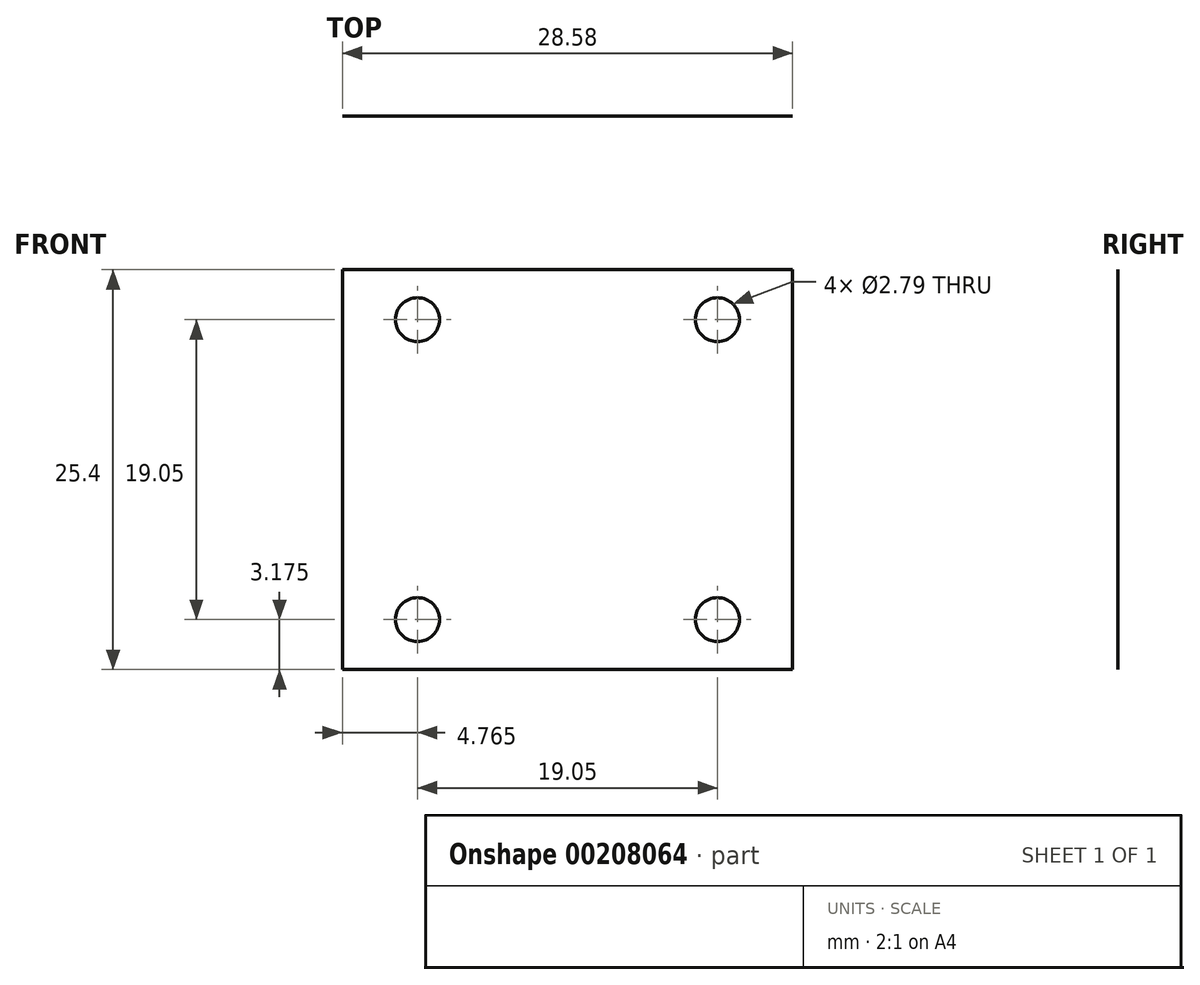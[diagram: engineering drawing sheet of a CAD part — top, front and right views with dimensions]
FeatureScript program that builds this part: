
annotation { "Feature Type Name" : "Feature", "Feature Type Description" : "" }
export const myFeature = defineFeature(function(context is Context, id is Id, definition is map)
    precondition{}
    {
        {
            var Q0;
            Q0=qCreatedBy(makeId("Front.planeOp"),FACE);
            var sketch = newSketch(context, id + "F0", { "sketchPlane" : qUnion([Q0])});
            skLineSegment(sketch, "E0.bottom", {"start": v(14.29, -12.7) * mm, "end": v(-14.29, -12.7) * mm});
            skLineSegment(sketch, "E0.top", {"start": v(14.29, 12.7) * mm, "end": v(-14.29, 12.7) * mm});
            skLineSegment(sketch, "E0.left", {"start": v(14.29, -12.7) * mm, "end": v(14.29, 12.7) * mm});
            skLineSegment(sketch, "E0.right", {"start": v(-14.29, -12.7) * mm, "end": v(-14.29, 12.7) * mm});
            skPoint(sketch, "E0.middle", {"position": v(0, 0) * mm});
            skSolve(sketch);
        }
        {
            var Q0;
            Q0=makeQuery(id+"F0.imprint","IMPRINT",FACE,{"disambiguationData":[TD([[makeQuery(id+"F0.imprint","IMPRINT",EDGE,{"derivedFrom":sQuery(id+"F0.wireOp",EDGE,"E0.bottom")}),-1.0]])]});
            extrude(context, id + "F1", {"entities" : qUnion([Q0]), "depth" : 1 / 203.2 * mm});
        }
        {
            var Q0;
            Q0=makeQuery(id+"F1.opExtrude","CAP_FACE",FACE,{"disambiguationData":[OSD([sQuery(id+"F0.wireOp",EDGE,"E0.bottom"),sQuery(id+"F0.wireOp",EDGE,"E0.top"),sQuery(id+"F0.wireOp",EDGE,"E0.left"),sQuery(id+"F0.wireOp",EDGE,"E0.right")])],"isStart":true});
            var sketch = newSketch(context, id + "F2", { "sketchPlane" : qUnion([Q0])});
            skPoint(sketch, "E1", {"position": v(9.52, -9.53) * mm});
            skPoint(sketch, "E2", {"position": v(-9.53, -9.53) * mm});
            skPoint(sketch, "E3", {"position": v(-9.53, 9.52) * mm});
            skPoint(sketch, "E4", {"position": v(9.52, 9.53) * mm});
            skLineSegment(sketch, "E5", {"start": v(9.53, -9.53) * mm, "end": v(9.53, -12.7) * mm});
            skLineSegment(sketch, "E6", {"start": v(9.52, 9.53) * mm, "end": v(9.52, 12.7) * mm});
            skLineSegment(sketch, "E7", {"start": v(-9.53, -9.53) * mm, "end": v(-14.29, -9.53) * mm});
            skLineSegment(sketch, "E8", {"start": v(9.53, -9.53) * mm, "end": v(14.29, -9.52) * mm});
            skSolve(sketch);
        }
        {
            var Q0;
            Q0=sQuery(id+"F2.wireOp",VERTEX,"E1");
            var Q1;
            Q1=sQuery(id+"F2.wireOp",VERTEX,"E2");
            var Q2;
            Q2=sQuery(id+"F2.wireOp",VERTEX,"E3");
            var Q3;
            Q3=sQuery(id+"F2.wireOp",VERTEX,"E4");
            var Q4;
            Q4=makeQuery(id+"F1.opExtrude","SWEPT_BODY",BODY,{"disambiguationData":[OSD([sQuery(id+"F0.wireOp",EDGE,"E0.bottom"),sQuery(id+"F0.wireOp",EDGE,"E0.top"),sQuery(id+"F0.wireOp",EDGE,"E0.left"),sQuery(id+"F0.wireOp",EDGE,"E0.right")])]});
            hole(context, id + "F3", {"style" : HoleStyle.SIMPLE, "endStyle" : HoleEndStyle.THROUGH, "standardTappedOrClearance" : lookupTablePath({ "standard" : "ANSI", "fit" : "Normal (ASME)", "size" : "#3", "type" : "Clearance" }), "standardBlindInLast" : lookupTablePath({ "fit" : "Free", "standard" : "ANSI", "size" : "#3", "type" : "Clearance" }), "holeDiameter" : 2.8 * mm, "tappedDepth" : 1.6 * mm, "tapClearance" : 3, "locations" : qUnion([Q0, Q1, Q2, Q3]), "scope" : qUnion([Q4])});
        }
    });
